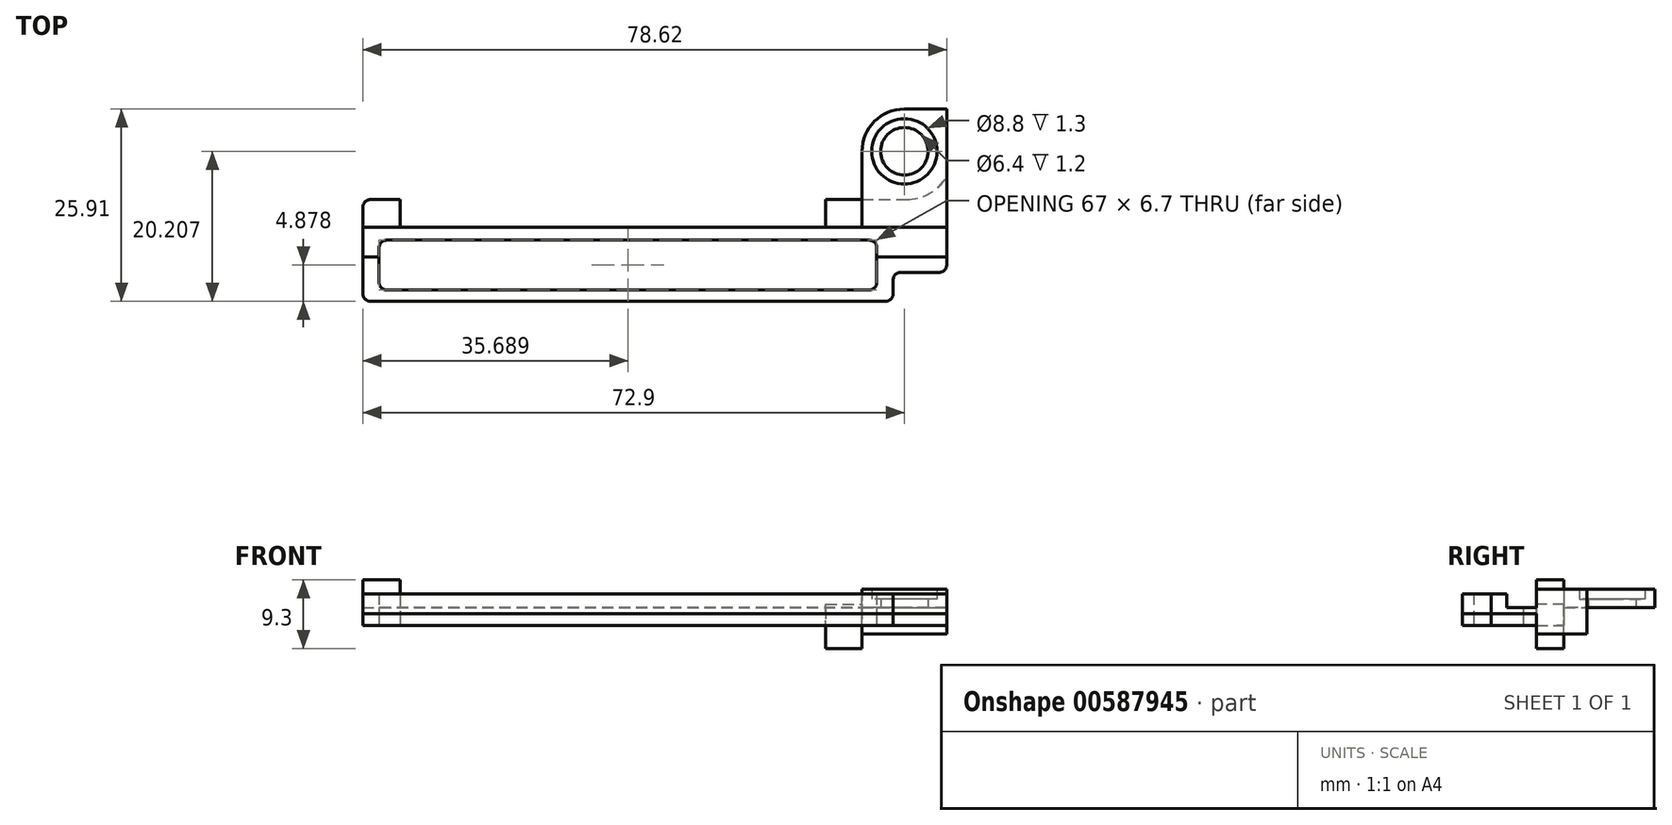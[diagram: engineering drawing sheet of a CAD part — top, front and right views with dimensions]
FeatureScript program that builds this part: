
annotation { "Feature Type Name" : "Feature", "Feature Type Description" : "" }
export const myFeature = defineFeature(function(context is Context, id is Id, definition is map)
    precondition{}
    {
        {
            var Q0;
            Q0=qCreatedBy(makeId("Top.planeOp"),FACE);
            var sketch = newSketch(context, id + "F0", { "sketchPlane" : qUnion([Q0])});
            skLineSegment(sketch, "E0.bottom", {"start": v(0, 6) * mm, "end": v(78.6, 6) * mm});
            skLineSegment(sketch, "E0.top", {"start": v(0, 0) * mm, "end": v(78.6, 0) * mm});
            skLineSegment(sketch, "E0.left", {"start": v(0, 6) * mm, "end": v(0, 0) * mm});
            skLineSegment(sketch, "E0.right", {"start": v(78.6, 6) * mm, "end": v(78.6, 0) * mm});
            skLineSegment(sketch, "E1.right", {"start": v(71.4, 0) * mm, "end": v(71.4, 3.9) * mm});
            skFitSpline(sketch, "E2", {"points": [v(0, 6) * mm, v(78.6, 6) * mm], "startDerivative": vector(78.6, 0) * mm, "endDerivative": vector(78.6, 0) * mm});
            skLineSegment(sketch, "E3.bottom", {"start": v(68, 3.9) * mm, "end": v(38, 3.9) * mm});
            skLineSegment(sketch, "E3.top", {"start": v(68, 1.9) * mm, "end": v(38, 1.9) * mm});
            skLineSegment(sketch, "E3.left", {"start": v(68, 3.9) * mm, "end": v(68, 1.9) * mm});
            skLineSegment(sketch, "E3.right", {"start": v(38, 3.9) * mm, "end": v(38, 1.9) * mm});
            skLineSegment(sketch, "E4", {"start": v(71.4, 3.9) * mm, "end": v(78.6, 3.9) * mm});
            skLineSegment(sketch, "E5.bottom", {"start": v(36.13, 3.9) * mm, "end": v(3.63, 3.9) * mm});
            skLineSegment(sketch, "E5.top", {"start": v(36.13, 1.9) * mm, "end": v(3.63, 1.9) * mm});
            skLineSegment(sketch, "E5.left", {"start": v(36.13, 3.9) * mm, "end": v(36.13, 1.9) * mm});
            skLineSegment(sketch, "E5.right", {"start": v(3.63, 3.9) * mm, "end": v(3.63, 1.9) * mm});
            skSolve(sketch);
        }
        {
            var Q0;
            {var subQ3=sQuery(id+"F0.wireOp",EDGE,"E0.left");Q0=makeQuery(id+"F0.imprint","IMPRINT",FACE,{"disambiguationData":[TD([[makeQuery(id+"F0.imprint","IMPRINT",EDGE,{"derivedFrom":subQ3}),1.0]])]});}
            extrude(context, id + "F1", {"entities" : qUnion([Q0]), "depth" : 1.4 * mm, "offsetDistance" : 25 * mm});
        }
        {
            var Q0;
            Q0=qCreatedBy(makeId("Top.planeOp"),FACE);
            var sketch = newSketch(context, id + "F2", { "sketchPlane" : qUnion([Q0])});
            skLineSegment(sketch, "E6.top", {"start": v(0, 0) * mm, "end": v(71.4, 0) * mm});
            skLineSegment(sketch, "E6.left", {"start": v(0, 10) * mm, "end": v(0, 0) * mm});
            skLineSegment(sketch, "E7.right", {"start": v(71.4, 3.9) * mm, "end": v(71.4, 0) * mm});
            skLineSegment(sketch, "E8", {"start": v(71.4, 3.9) * mm, "end": v(78.6, 3.9) * mm});
            skLineSegment(sketch, "E9.top", {"start": v(0, 10) * mm, "end": v(78.6, 10) * mm});
            skLineSegment(sketch, "E9.right", {"start": v(78.6, 3.9) * mm, "end": v(78.6, 10) * mm});
            skLineSegment(sketch, "E10.0.0", {"start": v(71.4, 0) * mm, "end": v(71.4, 3.9) * mm});
            skLineSegment(sketch, "E10.0.2", {"start": v(78.6, 3.9) * mm, "end": v(78.6, 6) * mm});
            skFitSpline(sketch, "E10.0.3", {"points": [v(78.6, 6) * mm, v(52.4, 6) * mm, v(26.2, 6) * mm, v(0, 6) * mm]});
            skLineSegment(sketch, "E10.0.4", {"start": v(0, 6) * mm, "end": v(0, 0) * mm});
            skFitSpline(sketch, "E11.0.3", {"points": [v(78.6, 6) * mm, v(52.4, 6) * mm, v(26.2, 6) * mm, v(0, 6) * mm]});
            skSolve(sketch);
        }
        {
            var Q0;
            Q0 = qSketchRegion(id + "F2", true);
            extrude(context, id + "F3", {"entities" : qUnion([Q0]), "operationType" : NewBodyOperationType.ADD, "depth" : -1.3 * mm, "offsetDistance" : 25 * mm});
        }
        {
            var Q0;
            Q0=makeQuery(id+"F3.opExtrude","CAP_FACE",FACE,{"disambiguationData":[OSD([sQuery(id+"F2.wireOp",EDGE,"E6.top"),sQuery(id+"F2.wireOp",EDGE,"E6.left"),sQuery(id+"F2.wireOp",EDGE,"E7.right"),sQuery(id+"F2.wireOp",EDGE,"E8"),sQuery(id+"F2.wireOp",EDGE,"E9.top"),sQuery(id+"F2.wireOp",EDGE,"E9.right")])],"isStart":false});
            extrude(context, id + "F4", {"entities" : qUnion([Q0]), "depth" : 1.6 * mm, "offsetDistance" : 25 * mm});
        }
        {
            var Q0;
            Q0=makeQuery(id+"F4.opExtrude","CAP_FACE",FACE,{"disambiguationData":[OSD([sQuery(id+"F2.wireOp",EDGE,"E6.top"),sQuery(id+"F2.wireOp",EDGE,"E6.left"),sQuery(id+"F2.wireOp",EDGE,"E7.right"),sQuery(id+"F2.wireOp",EDGE,"E8"),sQuery(id+"F2.wireOp",EDGE,"E9.top"),sQuery(id+"F2.wireOp",EDGE,"E9.right")])],"isStart":false});
            var sketch = newSketch(context, id + "F5", { "sketchPlane" : qUnion([Q0])});
            skLineSegment(sketch, "E12.bottom", {"start": v(2.19, -8.23) * mm, "end": v(69.19, -8.23) * mm});
            skLineSegment(sketch, "E12.top", {"start": v(2.19, -1.53) * mm, "end": v(69.19, -1.53) * mm});
            skLineSegment(sketch, "E12.left", {"start": v(2.19, -8.23) * mm, "end": v(2.19, -1.53) * mm});
            skLineSegment(sketch, "E12.right", {"start": v(69.19, -8.23) * mm, "end": v(69.19, -1.53) * mm});
            skSolve(sketch);
        }
        {
            var Q0;
            Q0=makeQuery(id+"F5.imprint","IMPRINT",FACE,{"disambiguationData":[TD([[makeQuery(id+"F5.imprint","IMPRINT",EDGE,{"derivedFrom":sQuery(id+"F5.wireOp",EDGE,"E12.bottom")}),1.0]])]});
            extrude(context, id + "F6", {"entities" : qUnion([Q0]), "operationType" : NewBodyOperationType.REMOVE, "endBound" : BoundingType.THROUGH_ALL, "oppositeDirection" : true, "depth" : 1.6 * mm, "offsetDistance" : 25 * mm});
        }
        {
            var Q0;
            Q0=qCreatedBy(makeId("Top.planeOp"),FACE);
            var sketch = newSketch(context, id + "F7", { "sketchPlane" : qUnion([Q0])});
            skLineSegment(sketch, "E13.bottom", {"start": v(0, 10) * mm, "end": v(5, 10) * mm});
            skLineSegment(sketch, "E13.top", {"start": v(0, 13.7) * mm, "end": v(5, 13.7) * mm});
            skLineSegment(sketch, "E13.left", {"start": v(0, 10) * mm, "end": v(0, 13.7) * mm});
            skLineSegment(sketch, "E13.right", {"start": v(5, 10) * mm, "end": v(5, 13.7) * mm});
            skSolve(sketch);
        }
        {
            var Q0;
            {var subQ0=sQuery(id+"F2.wireOp",EDGE,"E9.top");var subQ1=sQuery(id+"F2.wireOp",EDGE,"E6.left");var subQ2=sQuery(id+"F2.wireOp",EDGE,"E9.right");var subQ3=sQuery(id+"F2.wireOp",EDGE,"E10.0.2");var subQ4=sQuery(id+"F2.wireOp",EDGE,"E10.0.4");Q0=makeQuery(id+"F3.boolean.opBoolean","SPLIT",FACE,{"disambiguationData":[TD([makeQuery(id+"F1.opExtrude","SWEPT_FACE",FACE,{"disambiguationData":[OSD([sQuery(id+"F0.wireOp",EDGE,"E0.left")])]})])],"derivedFrom":makeQuery(id+"F3.opExtrude","CAP_FACE",FACE,{"disambiguationData":[OSD([subQ1,subQ0,subQ2,sQuery(id+"F2.wireOp",EDGE,"E10.0.0"),sQuery(id+"F2.wireOp",EDGE,"E8"),subQ3,subQ4,sQuery(id+"F2.wireOp",EDGE,"E6.top")])],"isStart":true})});}
            var sketch = newSketch(context, id + "F8", { "sketchPlane" : qUnion([Q0])});
            skLineSegment(sketch, "E14.bottom", {"start": v(62.3, 13.7) * mm, "end": v(67.2, 13.7) * mm});
            skLineSegment(sketch, "E14.top", {"start": v(62.3, 10) * mm, "end": v(67.2, 10) * mm});
            skLineSegment(sketch, "E14.left", {"start": v(62.3, 13.7) * mm, "end": v(62.3, 10) * mm});
            skLineSegment(sketch, "E14.right", {"start": v(67.2, 13.7) * mm, "end": v(67.2, 10) * mm});
            skSolve(sketch);
        }
        {
            var Q0;
            Q0=makeQuery(id+"F4.opExtrude","SWEPT_EDGE",EDGE,{"disambiguationData":[OSD([sQuery(id+"F2.wireOp",EDGE,"E10.0.0"),sQuery(id+"F2.wireOp",EDGE,"E6.top")])]});
            var Q1;
            Q1=makeQuery(id+"F3.opExtrude","SWEPT_EDGE",EDGE,{"disambiguationData":[OSD([sQuery(id+"F2.wireOp",EDGE,"E10.0.0"),sQuery(id+"F2.wireOp",EDGE,"E6.top")])]});
            var Q2;
            Q2=makeQuery(id+"F1.opExtrude","SWEPT_EDGE",EDGE,{"disambiguationData":[OSD([sQuery(id+"F0.wireOp",EDGE,"E0.top"),sQuery(id+"F0.wireOp",EDGE,"E1.right")])]});
            var Q3;
            Q3=makeQuery(id+"F1.opExtrude","SWEPT_EDGE",EDGE,{"disambiguationData":[OSD([sQuery(id+"F0.wireOp",EDGE,"E1.right"),sQuery(id+"F0.wireOp",EDGE,"E4")])]});
            var Q4;
            Q4=makeQuery(id+"F3.opExtrude","SWEPT_EDGE",EDGE,{"disambiguationData":[OSD([sQuery(id+"F2.wireOp",EDGE,"E10.0.0"),sQuery(id+"F2.wireOp",EDGE,"E8")])]});
            var Q5;
            Q5=makeQuery(id+"F4.opExtrude","SWEPT_EDGE",EDGE,{"disambiguationData":[OSD([sQuery(id+"F2.wireOp",EDGE,"E10.0.0"),sQuery(id+"F2.wireOp",EDGE,"E8")])]});
            var Q6;
            Q6=makeQuery(id+"F4.opExtrude","SWEPT_EDGE",EDGE,{"disambiguationData":[OSD([sQuery(id+"F2.wireOp",EDGE,"E8"),sQuery(id+"F2.wireOp",EDGE,"E10.0.2")])]});
            var Q7;
            Q7=makeQuery(id+"F3.opExtrude","SWEPT_EDGE",EDGE,{"disambiguationData":[OSD([sQuery(id+"F2.wireOp",EDGE,"E8"),sQuery(id+"F2.wireOp",EDGE,"E10.0.2")])]});
            var Q8;
            Q8=makeQuery(id+"F1.opExtrude","SWEPT_EDGE",EDGE,{"disambiguationData":[OSD([sQuery(id+"F0.wireOp",EDGE,"E0.right"),sQuery(id+"F0.wireOp",EDGE,"E4")])]});
            var Q9;
            Q9=makeQuery(id+"F1.opExtrude","SWEPT_EDGE",EDGE,{"disambiguationData":[OSD([sQuery(id+"F0.wireOp",EDGE,"E0.top"),sQuery(id+"F0.wireOp",EDGE,"E0.left")])]});
            var Q10;
            Q10=makeQuery(id+"F3.opExtrude","SWEPT_EDGE",EDGE,{"disambiguationData":[OSD([sQuery(id+"F2.wireOp",EDGE,"E10.0.4"),sQuery(id+"F2.wireOp",EDGE,"E6.top")])]});
            var Q11;
            Q11=makeQuery(id+"F4.opExtrude","SWEPT_EDGE",EDGE,{"disambiguationData":[OSD([sQuery(id+"F2.wireOp",EDGE,"E10.0.4"),sQuery(id+"F2.wireOp",EDGE,"E6.top")])]});
            var Q12;
            Q12=makeQuery(id+"F16.opExtrude","SWEPT_EDGE",EDGE,{"disambiguationData":[OSD([sQuery(id+"F7.wireOp",EDGE,"E13.top"),sQuery(id+"F7.wireOp",EDGE,"E13.left")])]});
            var Q13;
            Q13=makeQuery(id+"F6.boolean.opBoolean","COPY",EDGE,{"derivedFrom":makeQuery(id+"F6.opExtrude","SWEPT_EDGE",EDGE,{"disambiguationData":[OSD([sQuery(id+"F5.wireOp",EDGE,"E12.bottom"),sQuery(id+"F5.wireOp",EDGE,"E12.right")])]})});
            var Q14;
            Q14=makeQuery(id+"F6.boolean.opBoolean","COPY",EDGE,{"derivedFrom":makeQuery(id+"F6.opExtrude","SWEPT_EDGE",EDGE,{"disambiguationData":[OSD([sQuery(id+"F5.wireOp",EDGE,"E12.top"),sQuery(id+"F5.wireOp",EDGE,"E12.right")])]})});
            var Q15;
            Q15=makeQuery(id+"F6.boolean.opBoolean","COPY",EDGE,{"derivedFrom":makeQuery(id+"F6.opExtrude","SWEPT_EDGE",EDGE,{"disambiguationData":[OSD([sQuery(id+"F5.wireOp",EDGE,"E12.bottom"),sQuery(id+"F5.wireOp",EDGE,"E12.left")])]})});
            var Q16;
            Q16=makeQuery(id+"F6.boolean.opBoolean","COPY",EDGE,{"derivedFrom":makeQuery(id+"F6.opExtrude","SWEPT_EDGE",EDGE,{"disambiguationData":[OSD([sQuery(id+"F5.wireOp",EDGE,"E12.top"),sQuery(id+"F5.wireOp",EDGE,"E12.left")])]})});
            fillet(context, id + "F9", {"entities" : qUnion([Q0, Q1, Q2, Q3, Q4, Q5, Q6, Q7, Q8, Q9, Q10, Q11, Q12, Q13, Q14, Q15, Q16]), "radius" : 1 * mm, "tangentPropagation" : true, "allowEdgeOverflow" : false});
        }
        {
            var Q0;
            Q0=qCreatedBy(makeId("Top.planeOp"),FACE);
            var sketch = newSketch(context, id + "F10", { "sketchPlane" : qUnion([Q0])});
            skLineSegment(sketch, "E15", {"start": v(78.62, 16.78) * mm, "end": v(78.6, 10) * mm});
            skLineSegment(sketch, "E16.0", {"start": v(67.2, 13.7) * mm, "end": v(67.2, 10) * mm});
            skLineSegment(sketch, "E17", {"start": v(78.6, 10) * mm, "end": v(67.2, 10) * mm});
            skLineSegment(sketch, "E18", {"start": v(67.2, 13.7) * mm, "end": v(73.17, 13.7) * mm});
            skArc(sketch, "E19", {"start": v(73.17, 13.7) * mm, "mid": v(76.3, 14.53) * mm, "end": v(78.62, 16.78) * mm});
            skSolve(sketch);
        }
        {
            var Q0;
            Q0 = qSketchRegion(id + "F10", true);
            extrude(context, id + "F11", {"entities" : qUnion([Q0]), "oppositeDirection" : true, "depth" : 4 * mm, "offsetDistance" : 25 * mm});
        }
        {
            var Q0;
            Q0=qCreatedBy(makeId("Top.planeOp"),FACE);
            var sketch = newSketch(context, id + "F12", { "sketchPlane" : qUnion([Q0])});
            skLineSegment(sketch, "E20.bottom", {"start": v(72.9, 25.9) * mm, "end": v(78.6, 25.9) * mm});
            skLineSegment(sketch, "E20.left", {"start": v(67.2, 20.2) * mm, "end": v(67.2, 10) * mm});
            skLineSegment(sketch, "E20.right", {"start": v(78.6, 25.9) * mm, "end": v(78.6, 10) * mm});
            skCircle(sketch, "E21", {"center": v(72.9, 20.2) * mm, "radius": 3.2 * mm});
            skPoint(sketch, "E22.visualSharp", {"position": v(67.2, 25.9) * mm});
            skArc(sketch, "E22.filletArc", {"start": v(72.9, 25.9) * mm, "mid": v(68.87, 24.24) * mm, "end": v(67.2, 20.2) * mm});
            skCircle(sketch, "E23.0", {"center": v(72.9, 20.2) * mm, "radius": 4.4 * mm});
            skLineSegment(sketch, "E24", {"start": v(67.2, 10) * mm, "end": v(78.6, 10) * mm});
            skLineSegment(sketch, "E25.0", {"start": v(0, 0) * mm, "end": v(71.4, 0) * mm});
            skLineSegment(sketch, "E25.1", {"start": v(0, 10) * mm, "end": v(0, 0) * mm});
            skLineSegment(sketch, "E25.2", {"start": v(71.4, 3.9) * mm, "end": v(71.4, 0) * mm});
            skLineSegment(sketch, "E25.3", {"start": v(71.4, 3.9) * mm, "end": v(78.6, 3.9) * mm});
            skLineSegment(sketch, "E25.4", {"start": v(0, 10) * mm, "end": v(78.6, 10) * mm});
            skLineSegment(sketch, "E25.5", {"start": v(78.6, 3.9) * mm, "end": v(78.6, 10) * mm});
            skLineSegment(sketch, "E25.6", {"start": v(71.4, 0) * mm, "end": v(71.4, 3.9) * mm});
            skLineSegment(sketch, "E25.7", {"start": v(71.4, 3.9) * mm, "end": v(78.6, 3.9) * mm});
            skLineSegment(sketch, "E25.8", {"start": v(78.6, 3.9) * mm, "end": v(78.6, 6) * mm});
            skFitSpline(sketch, "E25.9", {"points": [v(78.6, 6) * mm, v(52.4, 6) * mm, v(26.2, 6) * mm, v(0, 6) * mm]});
            skLineSegment(sketch, "E25.10", {"start": v(0, 6) * mm, "end": v(0, 0) * mm});
            skLineSegment(sketch, "E25.11", {"start": v(0, 0) * mm, "end": v(71.4, 0) * mm});
            skLineSegment(sketch, "E25.12", {"start": v(71.4, 0) * mm, "end": v(71.4, 3.9) * mm});
            skLineSegment(sketch, "E25.13", {"start": v(71.4, 3.9) * mm, "end": v(78.6, 3.9) * mm});
            skLineSegment(sketch, "E25.14", {"start": v(78.6, 3.9) * mm, "end": v(78.6, 6) * mm});
            skFitSpline(sketch, "E25.15", {"points": [v(78.6, 6) * mm, v(52.4, 6) * mm, v(26.2, 6) * mm, v(0, 6) * mm]});
            skLineSegment(sketch, "E25.16", {"start": v(0, 6) * mm, "end": v(0, 0) * mm});
            skLineSegment(sketch, "E25.17", {"start": v(0, 0) * mm, "end": v(71.4, 0) * mm});
            skArc(sketch, "E25.18", {"start": v(73.17, 13.7) * mm, "mid": v(76.3, 14.53) * mm, "end": v(78.62, 16.78) * mm});
            skLineSegment(sketch, "E26.0", {"start": v(67.2, 13.7) * mm, "end": v(73.17, 13.7) * mm});
            skSolve(sketch);
        }
        {
            var Q0;
            Q0=makeQuery(id+"F12.imprint","IMPRINT",FACE,{"disambiguationData":[TD([[makeQuery(id+"F12.imprint","IMPRINT",EDGE,{"derivedFrom":sQuery(id+"F12.wireOp",EDGE,"E20.bottom")}),-1.0]])]});
            var Q1;
            Q1=makeQuery(id+"F10.imprint","IMPRINT",FACE,{"disambiguationData":[TD([[makeQuery(id+"F10.imprint","IMPRINT",EDGE,{"derivedFrom":sQuery(id+"F10.wireOp",EDGE,"E15")}),-1.0]])]});
            extrude(context, id + "F13", {"entities" : qUnion([Q0, Q1]), "operationType" : NewBodyOperationType.ADD, "depth" : 2 * mm, "offsetDistance" : 25 * mm});
        }
        {
            var Q0;
            Q0=makeQuery(id+"F12.imprint","IMPRINT",FACE,{"disambiguationData":[TD([[makeQuery(id+"F12.imprint","IMPRINT",EDGE,{"derivedFrom":sQuery(id+"F12.wireOp",EDGE,"E21")}),-1.0]])]});
            extrude(context, id + "F14", {"entities" : qUnion([Q0]), "operationType" : NewBodyOperationType.ADD, "depth" : 0.7 * mm, "offsetDistance" : 25 * mm});
        }
        {
            var Q0;
            {var subQ1=sQuery(id+"F12.wireOp",EDGE,"E20.bottom");Q0=makeQuery(id+"F12.imprint","IMPRINT",FACE,{"disambiguationData":[TD([[makeQuery(id+"F12.imprint","IMPRINT",EDGE,{"derivedFrom":subQ1}),-1.0]])]});}
            var Q1;
            Q1=makeQuery(id+"F12.imprint","IMPRINT",FACE,{"disambiguationData":[TD([[makeQuery(id+"F12.imprint","IMPRINT",EDGE,{"derivedFrom":sQuery(id+"F12.wireOp",EDGE,"E21")}),-1.0]])]});
            extrude(context, id + "F15", {"entities" : qUnion([Q0, Q1]), "operationType" : NewBodyOperationType.ADD, "oppositeDirection" : true, "depth" : 0.5 * mm, "offsetDistance" : 25 * mm});
        }
        {
            var Q0;
            Q0=makeQuery(id+"F7.imprint","IMPRINT",FACE,{"disambiguationData":[TD([[makeQuery(id+"F7.imprint","IMPRINT",EDGE,{"derivedFrom":sQuery(id+"F7.wireOp",EDGE,"E13.bottom")}),1.0]])]});
            extrude(context, id + "F16", {"entities" : qUnion([Q0]), "depth" : 3.3 * mm, "offsetDistance" : 25 * mm, "hasSecondDirection" : true, "secondDirectionOppositeDirection" : true, "secondDirectionDepth" : 2.9 * mm});
        }
        {
            var Q0;
            Q0=makeQuery(id+"F8.imprint","IMPRINT",FACE,{"disambiguationData":[TD([[makeQuery(id+"F8.imprint","IMPRINT",EDGE,{"derivedFrom":sQuery(id+"F8.wireOp",EDGE,"E14.bottom")}),-1.0]])]});
            extrude(context, id + "F17", {"entities" : qUnion([Q0]), "depth" : -6 * mm, "offsetDistance" : 25 * mm});
        }
        {
            var Q0;
            {var subQ0=sQuery(id+"F2.wireOp",EDGE,"E9.top");var subQ1=sQuery(id+"F2.wireOp",EDGE,"E6.left");var subQ2=sQuery(id+"F2.wireOp",EDGE,"E9.right");var subQ3=sQuery(id+"F2.wireOp",EDGE,"E10.0.2");var subQ4=sQuery(id+"F2.wireOp",EDGE,"E10.0.4");Q0=makeQuery(id+"F3.boolean.opBoolean","SPLIT",FACE,{"disambiguationData":[TD([makeQuery(id+"F1.opExtrude","SWEPT_FACE",FACE,{"disambiguationData":[OSD([sQuery(id+"F0.wireOp",EDGE,"E0.left")])]})])],"derivedFrom":makeQuery(id+"F3.opExtrude","CAP_FACE",FACE,{"disambiguationData":[OSD([subQ1,subQ0,subQ2,sQuery(id+"F2.wireOp",EDGE,"E10.0.0"),sQuery(id+"F2.wireOp",EDGE,"E8"),subQ3,subQ4,sQuery(id+"F2.wireOp",EDGE,"E6.top")])],"isStart":true})});}
            var sketch = newSketch(context, id + "F18", { "sketchPlane" : qUnion([Q0])});
            skLineSegment(sketch, "E27.0", {"start": v(0, 10) * mm, "end": v(0, 6) * mm});
            skLineSegment(sketch, "E28.0", {"start": v(0, 10) * mm, "end": v(78.6, 10) * mm});
            skFitSpline(sketch, "E29.0", {"points": [v(0, 6) * mm, v(26.2, 6) * mm, v(52.4, 6) * mm, v(78.6, 6) * mm]});
            skLineSegment(sketch, "E30.0", {"start": v(78.6, 6) * mm, "end": v(78.6, 10) * mm});
            skSolve(sketch);
        }
        {
            var Q0;
            Q0=makeQuery(id+"F18.imprint","IMPRINT",FACE,{"disambiguationData":[TD([[makeQuery(id+"F18.imprint","IMPRINT",EDGE,{"derivedFrom":sQuery(id+"F18.wireOp",EDGE,"E27.0")}),1.0]])]});
            extrude(context, id + "F19", {"entities" : qUnion([Q0]), "operationType" : NewBodyOperationType.REMOVE, "oppositeDirection" : true, "depth" : 0.5 * mm, "offsetDistance" : 25 * mm});
        }
        {
            var Q0;
            Q0=makeQuery(id+"F16.opExtrude","SWEPT_EDGE",EDGE,{"disambiguationData":[OSD([sQuery(id+"F7.wireOp",EDGE,"E13.top"),sQuery(id+"F7.wireOp",EDGE,"E13.left")])]});
            fillet(context, id + "F20", {"entities" : qUnion([Q0]), "radius" : 1 * mm, "tangentPropagation" : true, "allowEdgeOverflow" : false});
        }
    });
